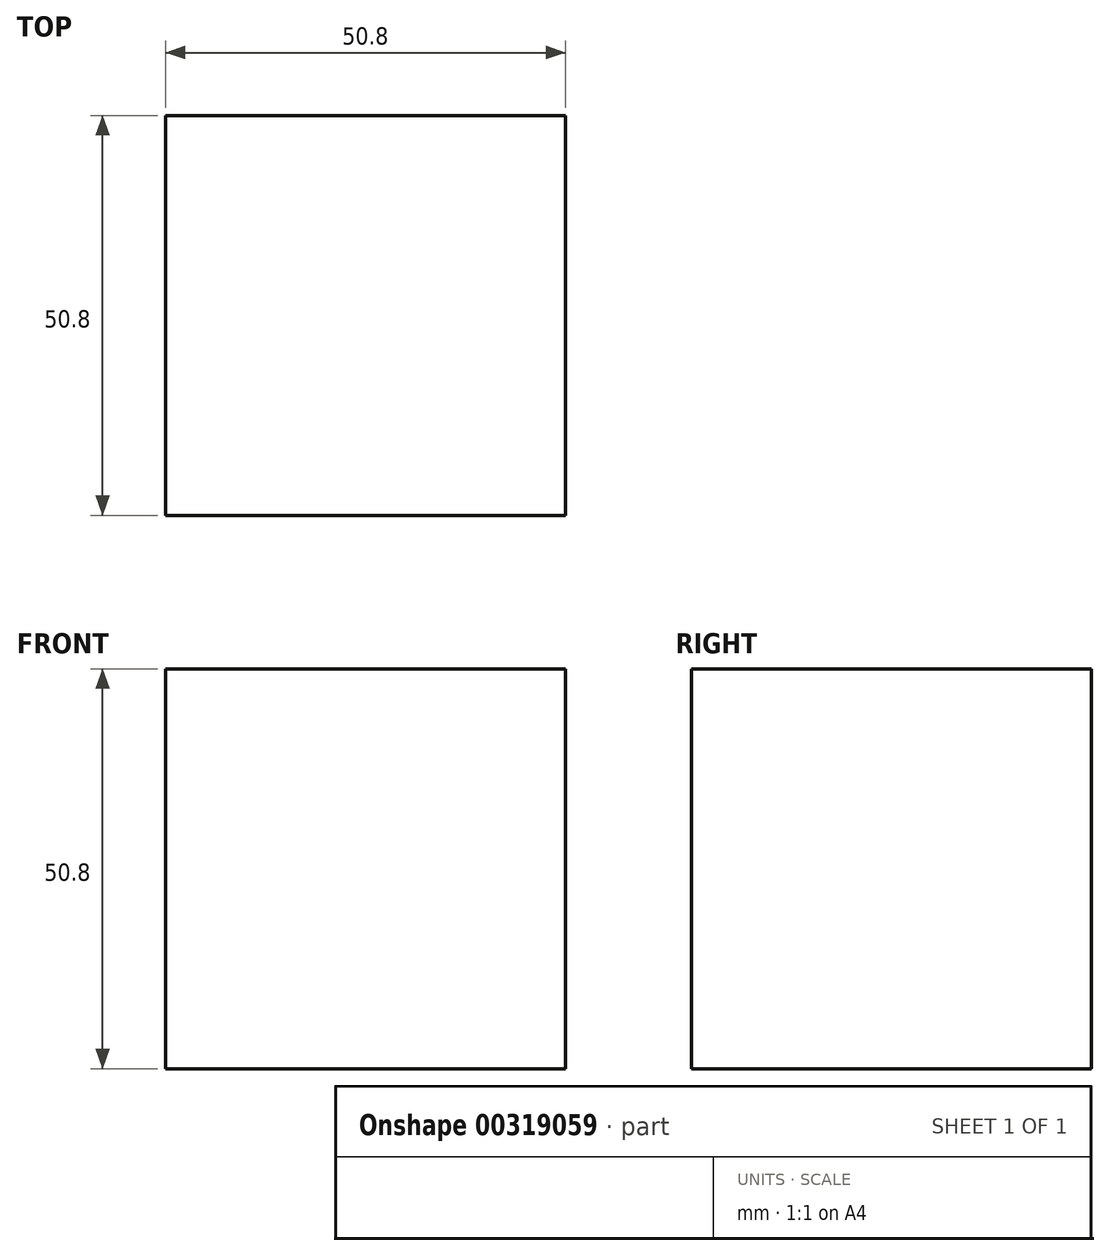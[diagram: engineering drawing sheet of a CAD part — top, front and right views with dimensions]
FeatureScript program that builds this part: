
annotation { "Feature Type Name" : "Feature", "Feature Type Description" : "" }
export const myFeature = defineFeature(function(context is Context, id is Id, definition is map)
    precondition{}
    {
        {
            var Q0;
            Q0=qCreatedBy(makeId("Front.planeOp"),FACE);
            var sketch = newSketch(context, id + "F0", { "sketchPlane" : qUnion([Q0])});
            skLineSegment(sketch, "E0.bottom", {"start": v(25.4, 25.4) * mm, "end": v(-25.4, 25.4) * mm});
            skLineSegment(sketch, "E0.top", {"start": v(25.4, -25.4) * mm, "end": v(-25.4, -25.4) * mm});
            skLineSegment(sketch, "E0.left", {"start": v(25.4, 25.4) * mm, "end": v(25.4, -25.4) * mm});
            skLineSegment(sketch, "E0.right", {"start": v(-25.4, 25.4) * mm, "end": v(-25.4, -25.4) * mm});
            skPoint(sketch, "E0.middle", {"position": v(0, 0) * mm});
            skLineSegment(sketch, "E1.bottom", {"start": v(-10.05, -25.4) * mm, "end": v(15.2, -25.4) * mm});
            skLineSegment(sketch, "E1.top", {"start": v(-10.05, -25.4) * mm, "end": v(15.2, -25.4) * mm});
            skLineSegment(sketch, "E1.left", {"start": v(-10.05, -25.4) * mm, "end": v(-10.05, -25.4) * mm});
            skLineSegment(sketch, "E1.right", {"start": v(15.2, -25.4) * mm, "end": v(15.2, -25.4) * mm});
            skPoint(sketch, "E1.middle", {"position": v(2.58, -25.4) * mm});
            skSolve(sketch);
        }
        {
            var Q0;
            Q0 = qSketchRegion(id + "F0", true);
            extrude(context, id + "F1", {"entities" : qUnion([Q0]), "depth" : 50.8 * mm});
        }
    });
